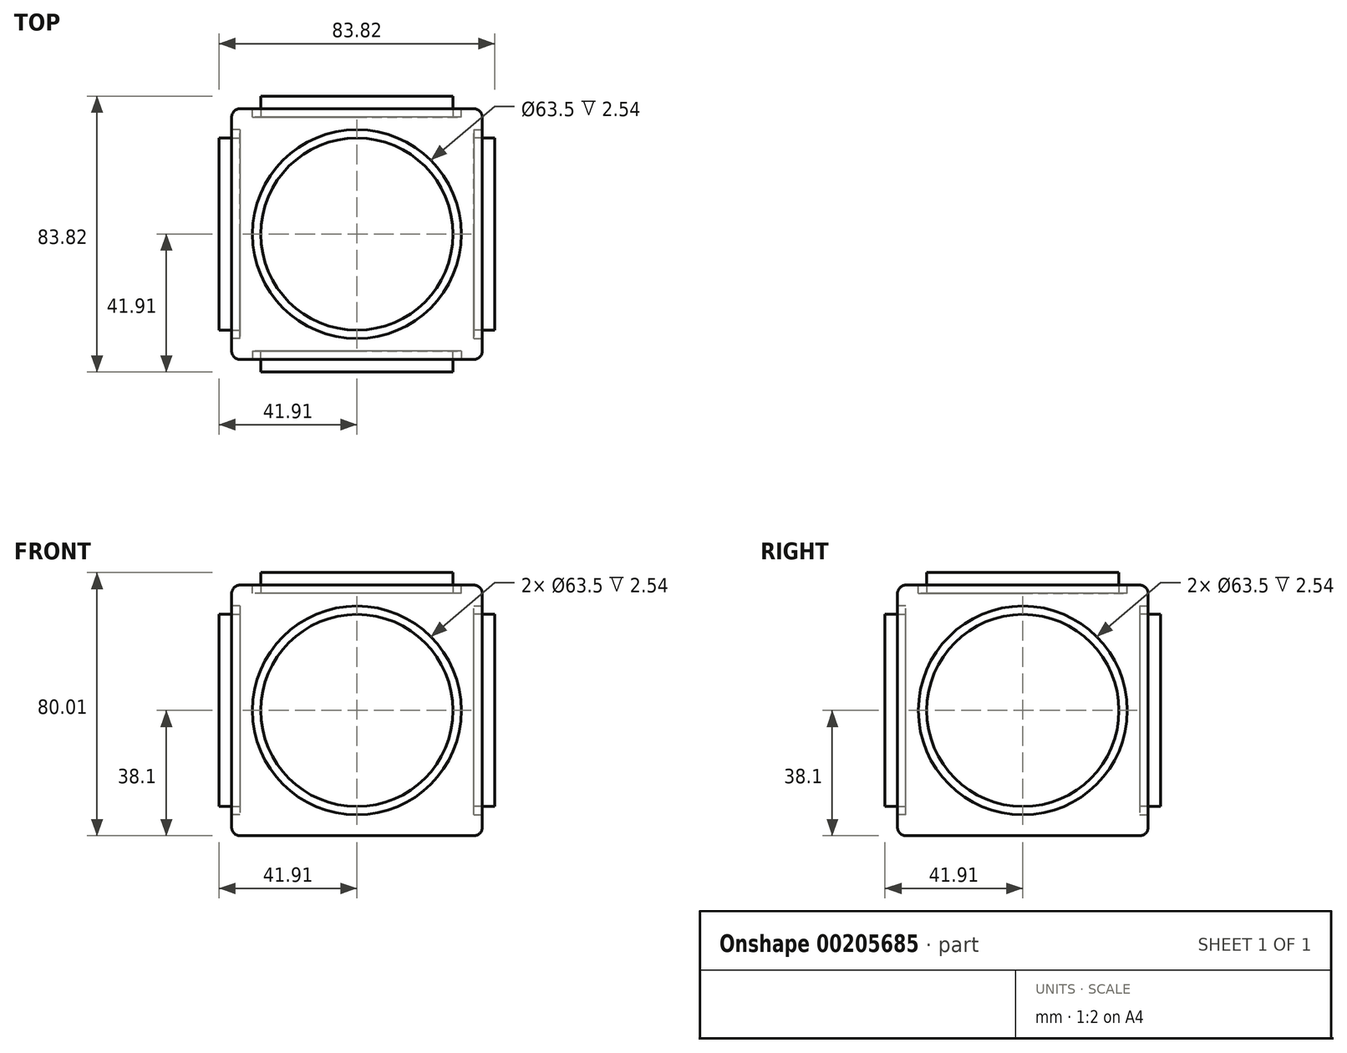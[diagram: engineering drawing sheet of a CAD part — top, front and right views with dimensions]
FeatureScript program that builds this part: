
annotation { "Feature Type Name" : "Feature", "Feature Type Description" : "" }
export const myFeature = defineFeature(function(context is Context, id is Id, definition is map)
    precondition{}
    {
        {
            var Q0;
            Q0=qCreatedBy(makeId("Top.planeOp"),FACE);
            var sketch = newSketch(context, id + "F0", { "sketchPlane" : qUnion([Q0])});
            skLineSegment(sketch, "E0.bottom", {"start": v(-38.1, -38.1) * mm, "end": v(38.1, -38.1) * mm});
            skLineSegment(sketch, "E0.top", {"start": v(-38.1, 38.1) * mm, "end": v(38.1, 38.1) * mm});
            skLineSegment(sketch, "E0.left", {"start": v(-38.1, -38.1) * mm, "end": v(-38.1, 38.1) * mm});
            skLineSegment(sketch, "E0.right", {"start": v(38.1, -38.1) * mm, "end": v(38.1, 38.1) * mm});
            skPoint(sketch, "E0.middle", {"position": v(0, 0) * mm});
            skSolve(sketch);
        }
        {
            var Q0;
            Q0 = qSketchRegion(id + "F0", true);
            extrude(context, id + "F1", {"entities" : qUnion([Q0]), "endBound" : BoundingType.SYMMETRIC, "depth" : 76.2 * mm});
        }
        {
            var Q0;
            Q0=makeQuery(id+"F1.opExtrude","CAP_FACE",FACE,{"disambiguationData":[OSD([sQuery(id+"F0.wireOp",EDGE,"E0.bottom"),sQuery(id+"F0.wireOp",EDGE,"E0.top"),sQuery(id+"F0.wireOp",EDGE,"E0.left"),sQuery(id+"F0.wireOp",EDGE,"E0.right")])],"isStart":false});
            var Q1;
            Q1=makeQuery(id+"F1.opExtrude","SWEPT_EDGE",EDGE,{"disambiguationData":[OSD([sQuery(id+"F0.wireOp",EDGE,"E0.bottom"),sQuery(id+"F0.wireOp",EDGE,"E0.right")])]});
            var Q2;
            Q2=makeQuery(id+"F1.opExtrude","SWEPT_FACE",FACE,{"disambiguationData":[OSD([sQuery(id+"F0.wireOp",EDGE,"E0.bottom")])]});
            var Q3;
            Q3=makeQuery(id+"F1.opExtrude","SWEPT_EDGE",EDGE,{"disambiguationData":[OSD([sQuery(id+"F0.wireOp",EDGE,"E0.bottom"),sQuery(id+"F0.wireOp",EDGE,"E0.left")])]});
            var Q4;
            Q4=makeQuery(id+"F1.opExtrude","SWEPT_FACE",FACE,{"disambiguationData":[OSD([sQuery(id+"F0.wireOp",EDGE,"E0.top")])]});
            var Q5;
            Q5=makeQuery(id+"F1.opExtrude","CAP_FACE",FACE,{"disambiguationData":[OSD([sQuery(id+"F0.wireOp",EDGE,"E0.bottom"),sQuery(id+"F0.wireOp",EDGE,"E0.top"),sQuery(id+"F0.wireOp",EDGE,"E0.left"),sQuery(id+"F0.wireOp",EDGE,"E0.right")])],"isStart":true});
            var Q6;
            Q6=makeQuery(id+"F1.opExtrude","CAP_EDGE",EDGE,{"disambiguationData":[OSD([sQuery(id+"F0.wireOp",EDGE,"E0.bottom")])],"isStart":true});
            var Q7;
            Q7=makeQuery(id+"F1.opExtrude","SWEPT_FACE",FACE,{"disambiguationData":[OSD([sQuery(id+"F0.wireOp",EDGE,"E0.left")])]});
            var Q8;
            Q8=makeQuery(id+"F1.opExtrude","CAP_EDGE",EDGE,{"disambiguationData":[OSD([sQuery(id+"F0.wireOp",EDGE,"E0.bottom")])],"isStart":false});
            var Q9;
            Q9=makeQuery(id+"F1.opExtrude","SWEPT_FACE",FACE,{"disambiguationData":[OSD([sQuery(id+"F0.wireOp",EDGE,"E0.right")])]});
            var Q10;
            Q10=makeQuery(id+"F1.opExtrude","SWEPT_EDGE",EDGE,{"disambiguationData":[OSD([sQuery(id+"F0.wireOp",EDGE,"E0.top"),sQuery(id+"F0.wireOp",EDGE,"E0.right")])]});
            var Q11;
            Q11=makeQuery(id+"F1.opExtrude","SWEPT_EDGE",EDGE,{"disambiguationData":[OSD([sQuery(id+"F0.wireOp",EDGE,"E0.top"),sQuery(id+"F0.wireOp",EDGE,"E0.left")])]});
            var Q12;
            Q12=makeQuery(id+"F1.opExtrude","CAP_EDGE",EDGE,{"disambiguationData":[OSD([sQuery(id+"F0.wireOp",EDGE,"E0.top")])],"isStart":true});
            var Q13;
            Q13=makeQuery(id+"F1.opExtrude","CAP_EDGE",EDGE,{"disambiguationData":[OSD([sQuery(id+"F0.wireOp",EDGE,"E0.top")])],"isStart":false});
            var Q14;
            Q14=makeQuery(id+"F1.opExtrude","CAP_EDGE",EDGE,{"disambiguationData":[OSD([sQuery(id+"F0.wireOp",EDGE,"E0.left")])],"isStart":true});
            var Q15;
            Q15=makeQuery(id+"F1.opExtrude","CAP_EDGE",EDGE,{"disambiguationData":[OSD([sQuery(id+"F0.wireOp",EDGE,"E0.left")])],"isStart":false});
            var Q16;
            Q16=makeQuery(id+"F1.opExtrude","CAP_EDGE",EDGE,{"disambiguationData":[OSD([sQuery(id+"F0.wireOp",EDGE,"E0.right")])],"isStart":true});
            var Q17;
            Q17=makeQuery(id+"F1.opExtrude","CAP_EDGE",EDGE,{"disambiguationData":[OSD([sQuery(id+"F0.wireOp",EDGE,"E0.right")])],"isStart":false});
            fillet(context, id + "F2", {"entities" : qUnion([Q0, Q1, Q2, Q3, Q4, Q5, Q6, Q7, Q8, Q9, Q10, Q11, Q12, Q13, Q14, Q15, Q16, Q17]), "radius" : 2.54 * mm, "tangentPropagation" : true, "allowEdgeOverflow" : false});
        }
        {
            var Q0;
            Q0=makeQuery(id+"F1.opExtrude","CAP_FACE",FACE,{"disambiguationData":[OSD([sQuery(id+"F0.wireOp",EDGE,"E0.bottom"),sQuery(id+"F0.wireOp",EDGE,"E0.top"),sQuery(id+"F0.wireOp",EDGE,"E0.left"),sQuery(id+"F0.wireOp",EDGE,"E0.right")])],"isStart":false});
            var sketch = newSketch(context, id + "F3", { "sketchPlane" : qUnion([Q0])});
            skCircle(sketch, "E1", {"center": v(0, 0) * mm, "radius": 31.75 * mm});
            skSolve(sketch);
        }
        {
            var Q0;
            Q0 = qSketchRegion(id + "F3", true);
            extrude(context, id + "F4", {"entities" : qUnion([Q0]), "operationType" : NewBodyOperationType.REMOVE, "oppositeDirection" : true, "depth" : 2.54 * mm});
        }
        {
            var Q0;
            Q0=makeQuery(id+"F4.boolean.opBoolean","COPY",FACE,{"derivedFrom":makeQuery(id+"F4.opExtrude","CAP_FACE",FACE,{"disambiguationData":[OSD([sQuery(id+"F3.wireOp",EDGE,"E1")])],"isStart":false})});
            var sketch = newSketch(context, id + "F5", { "sketchPlane" : qUnion([Q0])});
            skCircle(sketch, "E2", {"center": v(0, 0) * mm, "radius": 29.2 * mm});
            skSolve(sketch);
        }
        {
            var Q0;
            Q0 = qSketchRegion(id + "F5", true);
            extrude(context, id + "F6", {"entities" : qUnion([Q0]), "depth" : 6.35 * mm});
        }
        {
            var Q0;
            Q0=makeQuery(id+"F1.opExtrude","SWEPT_FACE",FACE,{"disambiguationData":[OSD([sQuery(id+"F0.wireOp",EDGE,"E0.left")])]});
            var sketch = newSketch(context, id + "F7", { "sketchPlane" : qUnion([Q0])});
            skCircle(sketch, "E3", {"center": v(0, 0) * mm, "radius": 31.75 * mm});
            skSolve(sketch);
        }
        {
            var Q0;
            Q0 = qSketchRegion(id + "F7", true);
            extrude(context, id + "F8", {"entities" : qUnion([Q0]), "operationType" : NewBodyOperationType.REMOVE, "oppositeDirection" : true, "depth" : 2.54 * mm});
        }
        {
            var Q0;
            Q0=makeQuery(id+"F8.boolean.opBoolean","COPY",FACE,{"derivedFrom":makeQuery(id+"F8.opExtrude","CAP_FACE",FACE,{"disambiguationData":[OSD([sQuery(id+"F7.wireOp",EDGE,"E3")])],"isStart":false})});
            var sketch = newSketch(context, id + "F9", { "sketchPlane" : qUnion([Q0])});
            skCircle(sketch, "E4", {"center": v(0, 0) * mm, "radius": 29.21 * mm});
            skSolve(sketch);
        }
        {
            var Q0;
            Q0 = qSketchRegion(id + "F9", true);
            extrude(context, id + "F10", {"entities" : qUnion([Q0]), "depth" : 6.35 * mm});
        }
        {
            var Q0;
            Q0=makeQuery(id+"F1.opExtrude","SWEPT_FACE",FACE,{"disambiguationData":[OSD([sQuery(id+"F0.wireOp",EDGE,"E0.right")])]});
            var sketch = newSketch(context, id + "F11", { "sketchPlane" : qUnion([Q0])});
            skCircle(sketch, "E5", {"center": v(0, 0) * mm, "radius": 31.75 * mm});
            skSolve(sketch);
        }
        {
            var Q0;
            Q0 = qSketchRegion(id + "F11", true);
            extrude(context, id + "F12", {"entities" : qUnion([Q0]), "operationType" : NewBodyOperationType.REMOVE, "oppositeDirection" : true, "depth" : 2.54 * mm});
        }
        {
            var Q0;
            Q0=makeQuery(id+"F1.opExtrude","SWEPT_FACE",FACE,{"disambiguationData":[OSD([sQuery(id+"F0.wireOp",EDGE,"E0.top")])]});
            var sketch = newSketch(context, id + "F13", { "sketchPlane" : qUnion([Q0])});
            skCircle(sketch, "E6", {"center": v(0, 0) * mm, "radius": 31.75 * mm});
            skSolve(sketch);
        }
        {
            var Q0;
            Q0 = qSketchRegion(id + "F13", true);
            extrude(context, id + "F14", {"entities" : qUnion([Q0]), "operationType" : NewBodyOperationType.REMOVE, "oppositeDirection" : true, "depth" : 2.54 * mm});
        }
        {
            var Q0;
            Q0=makeQuery(id+"F1.opExtrude","SWEPT_FACE",FACE,{"disambiguationData":[OSD([sQuery(id+"F0.wireOp",EDGE,"E0.bottom")])]});
            var sketch = newSketch(context, id + "F15", { "sketchPlane" : qUnion([Q0])});
            skCircle(sketch, "E7", {"center": v(0, 0) * mm, "radius": 31.75 * mm});
            skSolve(sketch);
        }
        {
            var Q0;
            Q0 = qSketchRegion(id + "F15", true);
            extrude(context, id + "F16", {"entities" : qUnion([Q0]), "operationType" : NewBodyOperationType.REMOVE, "oppositeDirection" : true, "depth" : 2.54 * mm});
        }
        {
            var Q0;
            Q0=makeQuery(id+"F12.boolean.opBoolean","COPY",FACE,{"derivedFrom":makeQuery(id+"F12.opExtrude","CAP_FACE",FACE,{"disambiguationData":[OSD([sQuery(id+"F11.wireOp",EDGE,"E5")])],"isStart":false})});
            var sketch = newSketch(context, id + "F17", { "sketchPlane" : qUnion([Q0])});
            skCircle(sketch, "E8", {"center": v(0, 0) * mm, "radius": 29.21 * mm});
            skSolve(sketch);
        }
        {
            var Q0;
            Q0 = qSketchRegion(id + "F17", true);
            extrude(context, id + "F18", {"entities" : qUnion([Q0]), "depth" : 6.35 * mm});
        }
        {
            var Q0;
            Q0=makeQuery(id+"F14.boolean.opBoolean","COPY",FACE,{"derivedFrom":makeQuery(id+"F14.opExtrude","CAP_FACE",FACE,{"disambiguationData":[OSD([sQuery(id+"F13.wireOp",EDGE,"E6")])],"isStart":false})});
            var sketch = newSketch(context, id + "F19", { "sketchPlane" : qUnion([Q0])});
            skCircle(sketch, "E9", {"center": v(0, 0) * mm, "radius": 29.21 * mm});
            skSolve(sketch);
        }
        {
            var Q0;
            Q0 = qSketchRegion(id + "F19", true);
            extrude(context, id + "F20", {"entities" : qUnion([Q0]), "depth" : 6.35 * mm});
        }
        {
            var Q0;
            Q0=makeQuery(id+"F16.boolean.opBoolean","COPY",FACE,{"derivedFrom":makeQuery(id+"F16.opExtrude","CAP_FACE",FACE,{"disambiguationData":[OSD([sQuery(id+"F15.wireOp",EDGE,"E7")])],"isStart":false})});
            var sketch = newSketch(context, id + "F21", { "sketchPlane" : qUnion([Q0])});
            skCircle(sketch, "E10", {"center": v(0, 0) * mm, "radius": 29.21 * mm});
            skSolve(sketch);
        }
        {
            var Q0;
            Q0 = qSketchRegion(id + "F21", true);
            extrude(context, id + "F22", {"entities" : qUnion([Q0]), "depth" : 6.35 * mm});
        }
    });
